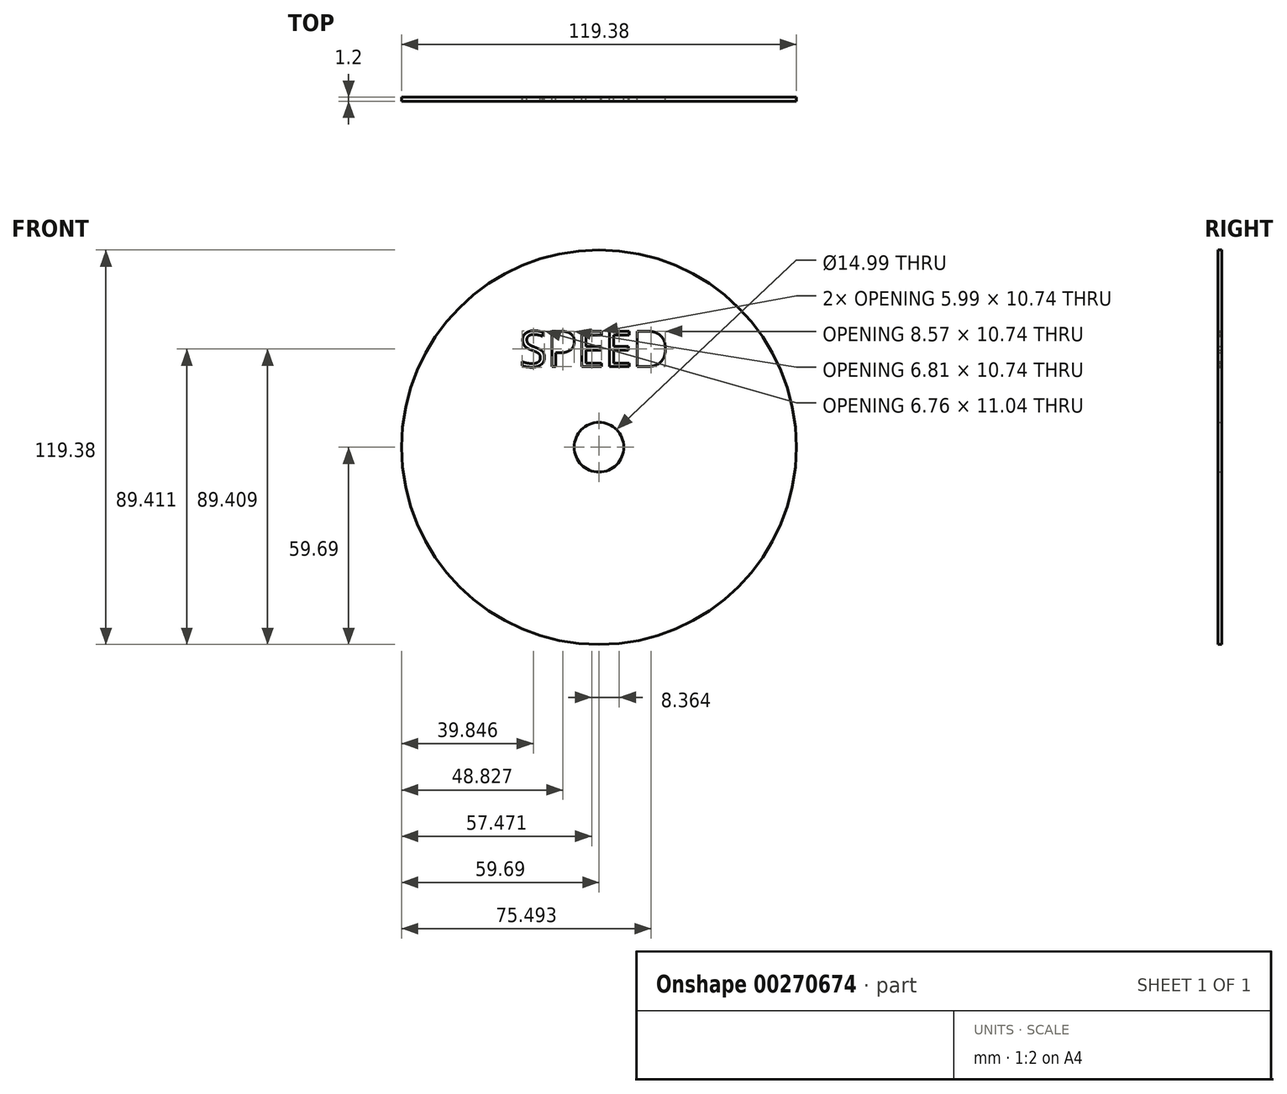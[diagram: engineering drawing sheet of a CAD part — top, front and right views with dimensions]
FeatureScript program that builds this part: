
annotation { "Feature Type Name" : "Feature", "Feature Type Description" : "" }
export const myFeature = defineFeature(function(context is Context, id is Id, definition is map)
    precondition{}
    {
        {
            var Q0;
            Q0=qCreatedBy(makeId("Front.planeOp"),FACE);
            var sketch = newSketch(context, id + "F0", { "sketchPlane" : qUnion([Q0])});
            skCircle(sketch, "E0", {"center": v(0, 0) * mm, "radius": 59.7 * mm});
            skCircle(sketch, "E1", {"center": v(0, 0) * mm, "radius": 7.5 * mm});
            skText(sketch, "E2", { "text": "SPEED\n", "fontName": "OpenSans-Regular.ttf"});
            const initialGuessF0  = {"E2": [-0.024, 0.02435, 1, 0, 0.01083]};
            skSetInitialGuess(sketch, initialGuessF0);
            skSolve(sketch);
        }
        {
            var Q0;
            Q0=makeQuery(id+"F0.imprint","IMPRINT",FACE,{"disambiguationData":[TD([[makeQuery(id+"F0.imprint","IMPRINT",EDGE,{"derivedFrom":sQuery(id+"F0.wireOp",EDGE,"E0")}),1.0]])]});
            extrude(context, id + "F1", {"entities" : qUnion([Q0]), "endBound" : BoundingType.SYMMETRIC, "depth" : 1.2 * mm});
        }
    });
